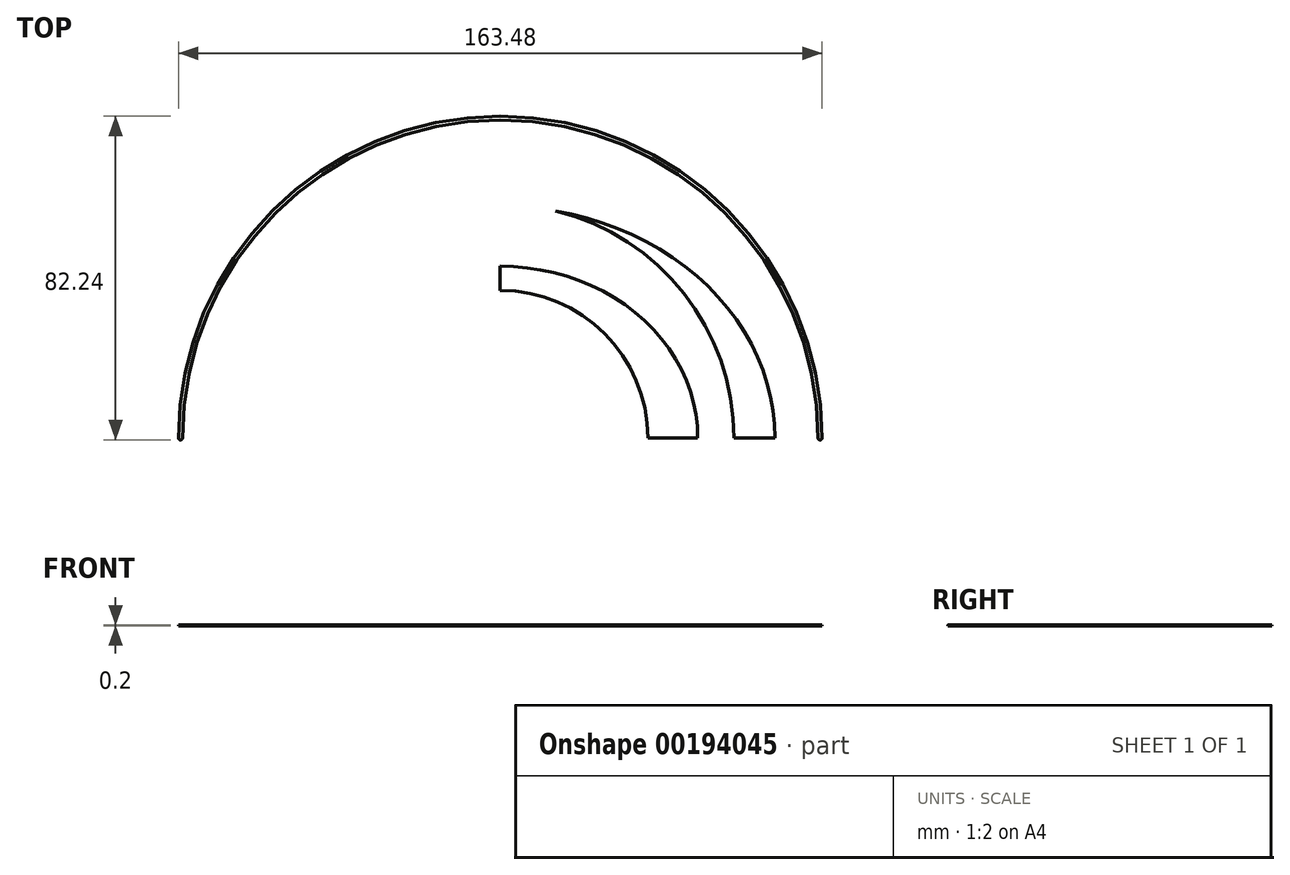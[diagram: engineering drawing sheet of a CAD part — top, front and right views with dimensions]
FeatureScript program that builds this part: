
annotation { "Feature Type Name" : "Feature", "Feature Type Description" : "" }
export const myFeature = defineFeature(function(context is Context, id is Id, definition is map)
    precondition{}
    {
        {
            var Q0;
            Q0=qCreatedBy(makeId("Top.planeOp"),FACE);
            var sketch = newSketch(context, id + "F0", { "sketchPlane" : qUnion([Q0])});
            skArc(sketch, "E0", {"start": v(-125, 0) * mm, "mid": v(0, 125) * mm, "end": v(125, 0) * mm});
            skArc(sketch, "E1", {"start": v(-81.24, 0) * mm, "mid": v(0, 81.24) * mm, "end": v(81.24, 0) * mm});
            skArc(sketch, "E2", {"start": v(-59.35, 0) * mm, "mid": v(0, 59.35) * mm, "end": v(59.35, 0) * mm});
            skArc(sketch, "E3", {"start": v(-37.47, 0) * mm, "mid": v(0, 37.47) * mm, "end": v(37.47, 0) * mm});
            skLineSegment(sketch, "E4", {"start": v(37.47, 0) * mm, "end": v(59.35, 0) * mm});
            skLineSegment(sketch, "E5", {"start": v(59.35, 0) * mm, "end": v(81.24, 0) * mm});
            skLineSegment(sketch, "E6", {"start": v(81.24, 0) * mm, "end": v(103.12, 0) * mm});
            skLineSegment(sketch, "E7", {"start": v(103.12, 0) * mm, "end": v(125, 0) * mm});
            skEllipticalArc(sketch, "E8", {});
            skEllipticalArc(sketch, "E9", {});
            skLineSegment(sketch, "E10", {"start": v(0, 0) * mm, "end": v(-125, 0) * mm});
            skEllipticalArc(sketch, "E11", {});
            skLineSegment(sketch, "E12", {"start": v(0, 0) * mm, "end": v(37.47, 0) * mm});
            skPoint(sketch, "E13", {"position": v(0, 27.98) * mm});
            skPoint(sketch, "E14", {"position": v(0, 37.47) * mm});
            skPoint(sketch, "E15", {"position": v(0, 49.86) * mm});
            skPoint(sketch, "E16", {"position": v(0, 59.35) * mm});
            skPoint(sketch, "E17", {"position": v(0, 71.74) * mm});
            skPoint(sketch, "E18", {"position": v(0, 81.24) * mm});
            skPoint(sketch, "E19", {"position": v(0, 93.62) * mm});
            skPoint(sketch, "E20", {"position": v(0, 125) * mm});
            skLineSegment(sketch, "E21", {"start": v(0, 81.24) * mm, "end": v(0, 93.62) * mm});
            skLineSegment(sketch, "E22", {"start": v(0, 59.35) * mm, "end": v(0, 71.74) * mm});
            skLineSegment(sketch, "E23", {"start": v(0, 37.47) * mm, "end": v(0, 49.86) * mm});
            skLineSegment(sketch, "E24", {"start": v(25.09, 0) * mm, "end": v(37.47, 0) * mm});
            skLineSegment(sketch, "E25", {"start": v(46.97, 0) * mm, "end": v(59.35, 0) * mm});
            skLineSegment(sketch, "E26", {"start": v(68.85, 0) * mm, "end": v(81.24, 0) * mm});
            skLineSegment(sketch, "E27", {"start": v(0, 71.74) * mm, "end": v(0, 49.86) * mm});
            skLineSegment(sketch, "E28", {"start": v(0, 27.98) * mm, "end": v(0, 49.86) * mm});
            const initialGuessF0  = {"E8": [0, 0, 1, 0, 0.0697578449369025, 0.05887321209295041, 0, 3.141592653589793], "E9": [0, 0, -1, 0, 0.05015816765465959, 0.04363105702985292, 3.141592653589793, 0], "E11": [0, 0, 1, 0, 0.03491601259156208, 0.028388901966755413, 0, 3.141592653589793], "E11": [0, 0, 1, 0, 0.01967385752846458, 0.01314674690365791, 0, 3.141592653589793]};
            skSetInitialGuess(sketch, initialGuessF0);
            skSolve(sketch);
        }
        {
            var Q0;
            Q0=qCreatedBy(makeId("Top.planeOp"),FACE);
            var sketch = newSketch(context, id + "F1", { "sketchPlane" : qUnion([Q0])});
            skEllipticalArc(sketch, "E29.0", {});
            skArc(sketch, "E30.0", {"start": v(-81.24, 0) * mm, "mid": v(0, 81.24) * mm, "end": v(81.24, 0) * mm});
            skEllipticalArc(sketch, "E31.0", {});
            skArc(sketch, "E32.0", {"start": v(-59.35, 0) * mm, "mid": v(0, 59.35) * mm, "end": v(59.35, 0) * mm});
            skEllipticalArc(sketch, "E33.0", {});
            skArc(sketch, "E34.0", {"start": v(-37.47, 0) * mm, "mid": v(0, 37.47) * mm, "end": v(37.47, 0) * mm});
            skArc(sketch, "E35.0.startCap", {"start": v(103.62, 0) * mm, "mid": v(103.12, -0.5) * mm, "end": v(102.62, 0) * mm});
            skArc(sketch, "E35.0.endCap", {"start": v(-102.62, 0) * mm, "mid": v(-103.12, -0.5) * mm, "end": v(-103.62, 0) * mm});
            skFitSpline(sketch, "E35.0.left", {"points": [v(82.49, -3.39) * mm, v(82.6, 0) * mm, v(82.49, 3.39) * mm, v(82.09, 7.87) * mm, v(81.09, 13.4) * mm, v(79.12, 19.87) * mm, v(76.4, 26.15) * mm, v(72.96, 32.17) * mm, v(69.5, 36.95) * mm, v(66.4, 40.6) * mm, v(63.9, 43.26) * mm, v(61.24, 45.81) * mm, v(58.41, 48.27) * mm, v(55.44, 50.6) * mm, v(52.36, 52.8) * mm, v(49.15, 54.87) * mm, v(44.73, 57.44) * mm, v(38.95, 60.3) * mm, v(31.66, 63.15) * mm, v(24.06, 65.4) * mm, v(17.53, 66.76) * mm, v(12.2, 67.53) * mm, v(8.17, 67.95) * mm, v(4.78, 68.15) * mm, v(2.05, 68.24) * mm, v(0, 68.26) * mm, v(-2.05, 68.24) * mm, v(-4.78, 68.15) * mm, v(-8.17, 67.95) * mm, v(-12.2, 67.53) * mm, v(-17.53, 66.76) * mm, v(-24.06, 65.4) * mm, v(-31.66, 63.15) * mm, v(-38.95, 60.3) * mm, v(-44.73, 57.44) * mm, v(-49.15, 54.87) * mm, v(-52.36, 52.8) * mm, v(-55.44, 50.6) * mm, v(-58.41, 48.27) * mm, v(-61.24, 45.81) * mm, v(-63.9, 43.26) * mm, v(-66.4, 40.6) * mm, v(-69.5, 36.95) * mm, v(-72.96, 32.17) * mm, v(-76.4, 26.15) * mm, v(-79.12, 19.87) * mm, v(-81.09, 13.4) * mm, v(-82.09, 7.87) * mm, v(-82.49, 3.39) * mm, v(-82.6, 0) * mm, v(-82.49, -3.39) * mm, v(-82.09, -7.87) * mm, v(-81.09, -13.4) * mm, v(-79.12, -19.87) * mm, v(-76.4, -26.15) * mm, v(-72.96, -32.17) * mm, v(-69.5, -36.95) * mm, v(-66.4, -40.6) * mm, v(-63.9, -43.26) * mm, v(-61.24, -45.81) * mm, v(-58.41, -48.27) * mm, v(-55.44, -50.6) * mm, v(-52.36, -52.8) * mm, v(-49.15, -54.87) * mm, v(-44.73, -57.44) * mm, v(-38.95, -60.3) * mm, v(-31.66, -63.15) * mm, v(-24.06, -65.4) * mm, v(-17.53, -66.76) * mm, v(-12.2, -67.53) * mm, v(-8.17, -67.95) * mm, v(-4.78, -68.15) * mm, v(-2.05, -68.24) * mm, v(0, -68.26) * mm, v(2.05, -68.24) * mm, v(4.78, -68.15) * mm, v(8.17, -67.95) * mm, v(12.2, -67.53) * mm, v(17.53, -66.76) * mm, v(24.06, -65.4) * mm, v(31.66, -63.15) * mm, v(38.95, -60.3) * mm, v(44.73, -57.44) * mm, v(49.15, -54.87) * mm, v(52.36, -52.8) * mm, v(55.44, -50.6) * mm, v(58.41, -48.27) * mm, v(61.24, -45.81) * mm, v(63.9, -43.26) * mm, v(66.4, -40.6) * mm, v(69.5, -36.95) * mm, v(72.96, -32.17) * mm, v(76.4, -26.15) * mm, v(79.12, -19.87) * mm, v(81.09, -13.4) * mm, v(82.09, -7.87) * mm, v(82.49, -3.39) * mm, v(82.6, 0) * mm, v(82.49, 3.39) * mm]});
            skFitSpline(sketch, "E35.0.right", {"points": [v(82.89, -3.41) * mm, v(83, 0) * mm, v(82.89, 3.41) * mm, v(82.48, 7.92) * mm, v(81.48, 13.5) * mm, v(79.5, 20.01) * mm, v(76.76, 26.33) * mm, v(73.3, 32.4) * mm, v(69.82, 37.2) * mm, v(66.7, 40.87) * mm, v(64.18, 43.54) * mm, v(61.51, 46.1) * mm, v(58.67, 48.58) * mm, v(55.68, 50.93) * mm, v(52.58, 53.14) * mm, v(49.36, 55.21) * mm, v(44.92, 57.8) * mm, v(39.1, 60.67) * mm, v(31.78, 63.53) * mm, v(24.16, 65.8) * mm, v(17.6, 67.16) * mm, v(12.25, 67.93) * mm, v(8.2, 68.34) * mm, v(4.8, 68.55) * mm, v(2.06, 68.64) * mm, v(0, 68.66) * mm, v(-2.06, 68.64) * mm, v(-4.8, 68.55) * mm, v(-8.2, 68.34) * mm, v(-12.25, 67.93) * mm, v(-17.6, 67.16) * mm, v(-24.16, 65.8) * mm, v(-31.78, 63.53) * mm, v(-39.1, 60.67) * mm, v(-44.92, 57.8) * mm, v(-49.36, 55.21) * mm, v(-52.58, 53.14) * mm, v(-55.68, 50.93) * mm, v(-58.67, 48.58) * mm, v(-61.51, 46.1) * mm, v(-64.18, 43.54) * mm, v(-66.7, 40.87) * mm, v(-69.82, 37.2) * mm, v(-73.3, 32.4) * mm, v(-76.76, 26.33) * mm, v(-79.5, 20.01) * mm, v(-81.48, 13.5) * mm, v(-82.48, 7.92) * mm, v(-82.89, 3.41) * mm, v(-83, 0) * mm, v(-82.89, -3.41) * mm, v(-82.48, -7.92) * mm, v(-81.48, -13.5) * mm, v(-79.5, -20.01) * mm, v(-76.76, -26.33) * mm, v(-73.3, -32.4) * mm, v(-69.82, -37.2) * mm, v(-66.7, -40.87) * mm, v(-64.18, -43.54) * mm, v(-61.51, -46.1) * mm, v(-58.67, -48.58) * mm, v(-55.68, -50.93) * mm, v(-52.58, -53.14) * mm, v(-49.36, -55.21) * mm, v(-44.92, -57.8) * mm, v(-39.1, -60.67) * mm, v(-31.78, -63.53) * mm, v(-24.16, -65.8) * mm, v(-17.6, -67.16) * mm, v(-12.25, -67.93) * mm, v(-8.2, -68.34) * mm, v(-4.8, -68.55) * mm, v(-2.06, -68.64) * mm, v(0, -68.66) * mm, v(2.06, -68.64) * mm, v(4.8, -68.55) * mm, v(8.2, -68.34) * mm, v(12.25, -67.93) * mm, v(17.6, -67.16) * mm, v(24.16, -65.8) * mm, v(31.78, -63.53) * mm, v(39.1, -60.67) * mm, v(44.92, -57.8) * mm, v(49.36, -55.21) * mm, v(52.58, -53.14) * mm, v(55.68, -50.93) * mm, v(58.67, -48.58) * mm, v(61.51, -46.1) * mm, v(64.18, -43.54) * mm, v(66.7, -40.87) * mm, v(69.82, -37.2) * mm, v(73.3, -32.4) * mm, v(76.76, -26.33) * mm, v(79.5, -20.01) * mm, v(81.48, -13.5) * mm, v(82.48, -7.92) * mm, v(82.89, -3.41) * mm, v(83, 0) * mm, v(82.89, 3.41) * mm]});
            skArc(sketch, "E35.3.startCap", {"start": v(-80.74, 0) * mm, "mid": v(-81.24, -0.5) * mm, "end": v(-81.74, 0) * mm});
            skArc(sketch, "E35.3.endCap", {"start": v(81.74, 0) * mm, "mid": v(81.24, -0.5) * mm, "end": v(80.74, 0) * mm});
            skArc(sketch, "E35.3.left", {"start": v(-81.74, 0) * mm, "mid": v(0, 81.74) * mm, "end": v(81.74, 0) * mm});
            skArc(sketch, "E35.3.right", {"start": v(-80.74, 0) * mm, "mid": v(0, 80.74) * mm, "end": v(80.74, 0) * mm});
            skArc(sketch, "E35.4.startCap", {"start": v(25.59, 0) * mm, "mid": v(25.09, -0.5) * mm, "end": v(24.59, 0) * mm});
            skArc(sketch, "E35.4.endCap", {"start": v(-24.59, 0) * mm, "mid": v(-25.09, -0.5) * mm, "end": v(-25.59, 0) * mm});
            skFitSpline(sketch, "E35.4.left", {"points": [v(13.24, -1.06) * mm, v(13.48, 0) * mm, v(13.24, 1.06) * mm, v(12.63, 1.94) * mm, v(11.89, 2.6) * mm, v(11, 3.25) * mm, v(9.6, 3.98) * mm, v(7.9, 4.59) * mm, v(6.37, 4.98) * mm, v(4.77, 5.3) * mm, v(3.08, 5.53) * mm, v(1.33, 5.64) * mm, v(0, 5.67) * mm, v(-1.33, 5.64) * mm, v(-3.08, 5.53) * mm, v(-4.77, 5.3) * mm, v(-6.37, 4.98) * mm, v(-7.9, 4.59) * mm, v(-9.6, 3.98) * mm, v(-11, 3.25) * mm, v(-11.89, 2.6) * mm, v(-12.63, 1.94) * mm, v(-13.24, 1.06) * mm, v(-13.48, 0) * mm, v(-13.24, -1.06) * mm, v(-12.63, -1.94) * mm, v(-11.89, -2.6) * mm, v(-11, -3.25) * mm, v(-9.6, -3.98) * mm, v(-7.9, -4.59) * mm, v(-6.37, -4.98) * mm, v(-4.77, -5.3) * mm, v(-3.08, -5.53) * mm, v(-1.33, -5.64) * mm, v(0, -5.67) * mm, v(1.33, -5.64) * mm, v(3.08, -5.53) * mm, v(4.77, -5.3) * mm, v(6.37, -4.98) * mm, v(7.9, -4.59) * mm, v(9.6, -3.98) * mm, v(11, -3.25) * mm, v(11.89, -2.6) * mm, v(12.63, -1.94) * mm, v(13.24, -1.06) * mm, v(13.48, 0) * mm, v(13.24, 1.06) * mm]});
            skFitSpline(sketch, "E35.4.right", {"points": [v(13.75, -0.62) * mm, v(13.82, 0) * mm, v(13.75, 0.62) * mm, v(13.47, 1.43) * mm, v(12.93, 2.2) * mm, v(12.14, 2.92) * mm, v(11.2, 3.6) * mm, v(9.76, 4.35) * mm, v(8.02, 4.97) * mm, v(6.46, 5.37) * mm, v(4.84, 5.7) * mm, v(3.12, 5.92) * mm, v(1.35, 6.04) * mm, v(0, 6.07) * mm, v(-1.35, 6.04) * mm, v(-3.12, 5.92) * mm, v(-4.84, 5.7) * mm, v(-6.46, 5.37) * mm, v(-8.02, 4.97) * mm, v(-9.76, 4.35) * mm, v(-11.2, 3.6) * mm, v(-12.14, 2.92) * mm, v(-12.93, 2.2) * mm, v(-13.47, 1.43) * mm, v(-13.75, 0.62) * mm, v(-13.82, 0) * mm, v(-13.75, -0.62) * mm, v(-13.47, -1.43) * mm, v(-12.93, -2.2) * mm, v(-12.14, -2.92) * mm, v(-11.2, -3.6) * mm, v(-9.76, -4.35) * mm, v(-8.02, -4.97) * mm, v(-6.46, -5.37) * mm, v(-4.84, -5.7) * mm, v(-3.12, -5.92) * mm, v(-1.35, -6.04) * mm, v(0, -6.07) * mm, v(1.35, -6.04) * mm, v(3.12, -5.92) * mm, v(4.84, -5.7) * mm, v(6.46, -5.37) * mm, v(8.02, -4.97) * mm, v(9.76, -4.35) * mm, v(11.2, -3.6) * mm, v(12.14, -2.92) * mm, v(12.93, -2.2) * mm, v(13.47, -1.43) * mm, v(13.75, -0.62) * mm, v(13.82, 0) * mm, v(13.75, 0.62) * mm]});
            skArc(sketch, "E35.5.startCap", {"start": v(69.35, 0) * mm, "mid": v(68.85, -0.5) * mm, "end": v(68.35, 0) * mm});
            skArc(sketch, "E35.5.endCap", {"start": v(-68.35, 0) * mm, "mid": v(-68.85, -0.5) * mm, "end": v(-69.35, 0) * mm});
            skFitSpline(sketch, "E35.5.left", {"points": [v(-55.09, 2.35) * mm, v(-55.15, 0) * mm, v(-55.09, -2.35) * mm, v(-54.82, -5.46) * mm, v(-54.15, -9.3) * mm, v(-52.83, -13.8) * mm, v(-51.02, -18.15) * mm, v(-48.72, -22.34) * mm, v(-45.95, -26.32) * mm, v(-43.27, -29.44) * mm, v(-40.9, -31.8) * mm, v(-39.01, -33.51) * mm, v(-37.03, -35.13) * mm, v(-34.28, -37.17) * mm, v(-30.64, -39.48) * mm, v(-26.01, -41.87) * mm, v(-21.14, -43.85) * mm, v(-16.07, -45.4) * mm, v(-10.83, -46.54) * mm, v(-6.36, -47.12) * mm, v(-2.74, -47.35) * mm, v(0, -47.4) * mm, v(2.74, -47.35) * mm, v(6.36, -47.12) * mm, v(10.83, -46.54) * mm, v(16.07, -45.4) * mm, v(21.14, -43.85) * mm, v(26.01, -41.87) * mm, v(30.64, -39.48) * mm, v(34.28, -37.17) * mm, v(37.03, -35.13) * mm, v(39.01, -33.51) * mm, v(40.9, -31.8) * mm, v(43.27, -29.44) * mm, v(45.95, -26.32) * mm, v(48.72, -22.34) * mm, v(51.02, -18.15) * mm, v(52.83, -13.8) * mm, v(54.15, -9.3) * mm, v(54.82, -5.46) * mm, v(55.09, -2.35) * mm, v(55.15, 0) * mm, v(55.09, 2.35) * mm, v(54.82, 5.46) * mm, v(54.15, 9.3) * mm, v(52.83, 13.8) * mm, v(51.02, 18.15) * mm, v(48.72, 22.34) * mm, v(45.95, 26.32) * mm, v(43.27, 29.44) * mm, v(40.9, 31.8) * mm, v(39.01, 33.51) * mm, v(37.03, 35.13) * mm, v(34.28, 37.17) * mm, v(30.64, 39.48) * mm, v(26.01, 41.87) * mm, v(21.14, 43.85) * mm, v(16.07, 45.4) * mm, v(10.83, 46.54) * mm, v(6.36, 47.12) * mm, v(2.74, 47.35) * mm, v(0, 47.4) * mm, v(-2.74, 47.35) * mm, v(-6.36, 47.12) * mm, v(-10.83, 46.54) * mm, v(-16.07, 45.4) * mm, v(-21.14, 43.85) * mm, v(-26.01, 41.87) * mm, v(-30.64, 39.48) * mm, v(-34.28, 37.17) * mm, v(-37.03, 35.13) * mm, v(-39.01, 33.51) * mm, v(-40.9, 31.8) * mm, v(-43.27, 29.44) * mm, v(-45.95, 26.32) * mm, v(-48.72, 22.34) * mm, v(-51.02, 18.15) * mm, v(-52.83, 13.8) * mm, v(-54.15, 9.3) * mm, v(-54.82, 5.46) * mm, v(-55.09, 2.35) * mm, v(-55.15, 0) * mm, v(-55.09, -2.35) * mm]});
            skFitSpline(sketch, "E35.5.right", {"points": [v(-55.49, 2.37) * mm, v(-55.55, 0) * mm, v(-55.49, -2.37) * mm, v(-55.21, -5.51) * mm, v(-54.54, -9.4) * mm, v(-53.21, -13.93) * mm, v(-51.38, -18.33) * mm, v(-49.06, -22.55) * mm, v(-46.27, -26.56) * mm, v(-43.56, -29.71) * mm, v(-41.17, -32.1) * mm, v(-39.27, -33.81) * mm, v(-37.27, -35.45) * mm, v(-34.5, -37.5) * mm, v(-30.84, -39.83) * mm, v(-26.18, -42.23) * mm, v(-21.27, -44.22) * mm, v(-16.17, -45.8) * mm, v(-10.9, -46.94) * mm, v(-6.4, -47.51) * mm, v(-2.76, -47.75) * mm, v(0, -47.8) * mm, v(2.76, -47.75) * mm, v(6.4, -47.51) * mm, v(10.9, -46.94) * mm, v(16.17, -45.8) * mm, v(21.27, -44.22) * mm, v(26.18, -42.23) * mm, v(30.84, -39.83) * mm, v(34.5, -37.5) * mm, v(37.27, -35.45) * mm, v(39.27, -33.81) * mm, v(41.17, -32.1) * mm, v(43.56, -29.71) * mm, v(46.27, -26.56) * mm, v(49.06, -22.55) * mm, v(51.38, -18.33) * mm, v(53.21, -13.93) * mm, v(54.54, -9.4) * mm, v(55.21, -5.51) * mm, v(55.49, -2.37) * mm, v(55.55, 0) * mm, v(55.49, 2.37) * mm, v(55.21, 5.51) * mm, v(54.54, 9.4) * mm, v(53.21, 13.93) * mm, v(51.38, 18.33) * mm, v(49.06, 22.55) * mm, v(46.27, 26.56) * mm, v(43.56, 29.71) * mm, v(41.17, 32.1) * mm, v(39.27, 33.81) * mm, v(37.27, 35.45) * mm, v(34.5, 37.5) * mm, v(30.84, 39.83) * mm, v(26.18, 42.23) * mm, v(21.27, 44.22) * mm, v(16.17, 45.8) * mm, v(10.9, 46.94) * mm, v(6.4, 47.51) * mm, v(2.76, 47.75) * mm, v(0, 47.8) * mm, v(-2.76, 47.75) * mm, v(-6.4, 47.51) * mm, v(-10.9, 46.94) * mm, v(-16.17, 45.8) * mm, v(-21.27, 44.22) * mm, v(-26.18, 42.23) * mm, v(-30.84, 39.83) * mm, v(-34.5, 37.5) * mm, v(-37.27, 35.45) * mm, v(-39.27, 33.81) * mm, v(-41.17, 32.1) * mm, v(-43.56, 29.71) * mm, v(-46.27, 26.56) * mm, v(-49.06, 22.55) * mm, v(-51.38, 18.33) * mm, v(-53.21, 13.93) * mm, v(-54.54, 9.4) * mm, v(-55.21, 5.51) * mm, v(-55.49, 2.37) * mm, v(-55.55, 0) * mm, v(-55.49, -2.37) * mm]});
            skArc(sketch, "E35.6.startCap", {"start": v(-36.97, 0) * mm, "mid": v(-37.47, -0.5) * mm, "end": v(-37.97, 0) * mm});
            skArc(sketch, "E35.6.endCap", {"start": v(37.97, 0) * mm, "mid": v(37.47, -0.5) * mm, "end": v(36.97, 0) * mm});
            skArc(sketch, "E35.6.left", {"start": v(-37.97, 0) * mm, "mid": v(0, 37.97) * mm, "end": v(37.97, 0) * mm});
            skArc(sketch, "E35.6.right", {"start": v(-36.97, 0) * mm, "mid": v(0, 36.97) * mm, "end": v(36.97, 0) * mm});
            skArc(sketch, "E35.7.startCap", {"start": v(-58.85, 0) * mm, "mid": v(-59.35, -0.5) * mm, "end": v(-59.85, 0) * mm});
            skArc(sketch, "E35.7.endCap", {"start": v(59.85, 0) * mm, "mid": v(59.35, -0.5) * mm, "end": v(58.85, 0) * mm});
            skArc(sketch, "E35.7.left", {"start": v(-59.85, 0) * mm, "mid": v(0, 59.85) * mm, "end": v(59.85, 0) * mm});
            skArc(sketch, "E35.7.right", {"start": v(-58.85, 0) * mm, "mid": v(0, 58.85) * mm, "end": v(58.85, 0) * mm});
            skArc(sketch, "E35.8.startCap", {"start": v(47.47, 0) * mm, "mid": v(46.97, -0.5) * mm, "end": v(46.47, 0) * mm});
            skArc(sketch, "E35.8.endCap", {"start": v(-46.47, 0) * mm, "mid": v(-46.97, -0.5) * mm, "end": v(-47.47, 0) * mm});
            skFitSpline(sketch, "E35.8.left", {"points": [v(34.24, -1.31) * mm, v(34.28, 0) * mm, v(34.24, 1.31) * mm, v(34.07, 3.05) * mm, v(33.66, 5.2) * mm, v(32.84, 7.71) * mm, v(31.72, 10.15) * mm, v(30.29, 12.49) * mm, v(28.57, 14.72) * mm, v(26.9, 16.47) * mm, v(25.43, 17.79) * mm, v(24.26, 18.74) * mm, v(23.03, 19.65) * mm, v(21.32, 20.8) * mm, v(19.06, 22.1) * mm, v(16.18, 23.43) * mm, v(13.15, 24.54) * mm, v(10, 25.41) * mm, v(6.74, 26.05) * mm, v(3.96, 26.37) * mm, v(1.7, 26.5) * mm, v(0, 26.53) * mm, v(-1.7, 26.5) * mm, v(-3.96, 26.37) * mm, v(-6.74, 26.05) * mm, v(-10, 25.41) * mm, v(-13.15, 24.54) * mm, v(-16.18, 23.43) * mm, v(-19.06, 22.1) * mm, v(-21.32, 20.8) * mm, v(-23.03, 19.65) * mm, v(-24.26, 18.74) * mm, v(-25.43, 17.79) * mm, v(-26.9, 16.47) * mm, v(-28.57, 14.72) * mm, v(-30.29, 12.49) * mm, v(-31.72, 10.15) * mm, v(-32.84, 7.71) * mm, v(-33.66, 5.2) * mm, v(-34.07, 3.05) * mm, v(-34.24, 1.31) * mm, v(-34.28, 0) * mm, v(-34.24, -1.31) * mm, v(-34.07, -3.05) * mm, v(-33.66, -5.2) * mm, v(-32.84, -7.71) * mm, v(-31.72, -10.15) * mm, v(-30.29, -12.49) * mm, v(-28.57, -14.72) * mm, v(-26.9, -16.47) * mm, v(-25.43, -17.79) * mm, v(-24.26, -18.74) * mm, v(-23.03, -19.65) * mm, v(-21.32, -20.8) * mm, v(-19.06, -22.1) * mm, v(-16.18, -23.43) * mm, v(-13.15, -24.54) * mm, v(-10, -25.41) * mm, v(-6.74, -26.05) * mm, v(-3.96, -26.37) * mm, v(-1.7, -26.5) * mm, v(0, -26.53) * mm, v(1.7, -26.5) * mm, v(3.96, -26.37) * mm, v(6.74, -26.05) * mm, v(10, -25.41) * mm, v(13.15, -24.54) * mm, v(16.18, -23.43) * mm, v(19.06, -22.1) * mm, v(21.32, -20.8) * mm, v(23.03, -19.65) * mm, v(24.26, -18.74) * mm, v(25.43, -17.79) * mm, v(26.9, -16.47) * mm, v(28.57, -14.72) * mm, v(30.29, -12.49) * mm, v(31.72, -10.15) * mm, v(32.84, -7.71) * mm, v(33.66, -5.2) * mm, v(34.07, -3.05) * mm, v(34.24, -1.31) * mm, v(34.28, 0) * mm, v(34.24, 1.31) * mm]});
            skFitSpline(sketch, "E35.8.right", {"points": [v(34.64, -1.34) * mm, v(34.68, 0) * mm, v(34.64, 1.34) * mm, v(34.47, 3.11) * mm, v(34.04, 5.3) * mm, v(33.21, 7.86) * mm, v(32.07, 10.34) * mm, v(30.62, 12.72) * mm, v(28.87, 14.98) * mm, v(27.18, 16.75) * mm, v(25.7, 18.1) * mm, v(24.5, 19.06) * mm, v(23.26, 19.98) * mm, v(21.53, 21.14) * mm, v(19.24, 22.45) * mm, v(16.33, 23.8) * mm, v(13.27, 24.92) * mm, v(10.09, 25.8) * mm, v(6.8, 26.44) * mm, v(4, 26.77) * mm, v(1.72, 26.9) * mm, v(0, 26.93) * mm, v(-1.72, 26.9) * mm, v(-4, 26.77) * mm, v(-6.8, 26.44) * mm, v(-10.09, 25.8) * mm, v(-13.27, 24.92) * mm, v(-16.33, 23.8) * mm, v(-19.24, 22.45) * mm, v(-21.53, 21.14) * mm, v(-23.26, 19.98) * mm, v(-24.5, 19.06) * mm, v(-25.7, 18.1) * mm, v(-27.18, 16.75) * mm, v(-28.87, 14.98) * mm, v(-30.62, 12.72) * mm, v(-32.07, 10.34) * mm, v(-33.21, 7.86) * mm, v(-34.04, 5.3) * mm, v(-34.47, 3.11) * mm, v(-34.64, 1.34) * mm, v(-34.68, 0) * mm, v(-34.64, -1.34) * mm, v(-34.47, -3.11) * mm, v(-34.04, -5.3) * mm, v(-33.21, -7.86) * mm, v(-32.07, -10.34) * mm, v(-30.62, -12.72) * mm, v(-28.87, -14.98) * mm, v(-27.18, -16.75) * mm, v(-25.7, -18.1) * mm, v(-24.5, -19.06) * mm, v(-23.26, -19.98) * mm, v(-21.53, -21.14) * mm, v(-19.24, -22.45) * mm, v(-16.33, -23.8) * mm, v(-13.27, -24.92) * mm, v(-10.09, -25.8) * mm, v(-6.8, -26.44) * mm, v(-4, -26.77) * mm, v(-1.72, -26.9) * mm, v(0, -26.93) * mm, v(1.72, -26.9) * mm, v(4, -26.77) * mm, v(6.8, -26.44) * mm, v(10.09, -25.8) * mm, v(13.27, -24.92) * mm, v(16.33, -23.8) * mm, v(19.24, -22.45) * mm, v(21.53, -21.14) * mm, v(23.26, -19.98) * mm, v(24.5, -19.06) * mm, v(25.7, -18.1) * mm, v(27.18, -16.75) * mm, v(28.87, -14.98) * mm, v(30.62, -12.72) * mm, v(32.07, -10.34) * mm, v(33.21, -7.86) * mm, v(34.04, -5.3) * mm, v(34.47, -3.11) * mm, v(34.64, -1.34) * mm, v(34.68, 0) * mm, v(34.64, 1.34) * mm]});
            const initialGuessF1  = {"E29.0": [0, 0, 1, 0, 0.08275722200183241, 0.06845269549475103, 0, 3.141592653589793], "E31.0": [0, 0, -1, 0, 0.055330932086608546, 0.0475872872835984, 3.141592653589793, 0], "E33.0": [0, 0, 1, 0, 0.03446552387545592, 0.026721879072445772, 0, 3.141592653589793], "E33.0": [0, 0, 1, 0, 0.013600115664303296, 0.0058564708612931435, 0, 3.141592653589793]};
            skSetInitialGuess(sketch, initialGuessF1);
            skSolve(sketch);
        }
        {
            var Q0;
            {var subQ0=sQuery(id+"F0.wireOp",EDGE,"E24");Q0=makeQuery(id+"F0.imprint","IMPRINT",FACE,{"disambiguationData":[TD([[makeQuery(id+"F0.imprint","IMPRINT",EDGE,{"derivedFrom":subQ0}),1.0]])]});}
            var Q1;
            {var subQ0=sQuery(id+"F0.wireOp",EDGE,"E4");Q1=makeQuery(id+"F0.imprint","IMPRINT",FACE,{"disambiguationData":[TD([[makeQuery(id+"F0.imprint","IMPRINT",EDGE,{"derivedFrom":subQ0}),1.0]])]});}
            var Q2;
            {var subQ0=sQuery(id+"F0.wireOp",EDGE,"E25");Q2=makeQuery(id+"F0.imprint","IMPRINT",FACE,{"disambiguationData":[TD([[makeQuery(id+"F0.imprint","IMPRINT",EDGE,{"derivedFrom":subQ0}),1.0]])]});}
            var Q3;
            {var subQ0=sQuery(id+"F0.wireOp",EDGE,"E5");Q3=makeQuery(id+"F0.imprint","IMPRINT",FACE,{"disambiguationData":[TD([[makeQuery(id+"F0.imprint","IMPRINT",EDGE,{"derivedFrom":subQ0}),1.0]])]});}
            var Q4;
            {var subQ0=sQuery(id+"F0.wireOp",EDGE,"E10");var subQ1=sQuery(id+"F0.wireOp",EDGE,"E2");var subQ2=makeQuery(id+"F0.imprint","INTERSECT",VERTEX,{"derivedFrom":[subQ1,subQ0]});Q4=makeQuery(id+"F0.imprint","IMPRINT",FACE,{"disambiguationData":[TD([[makeQuery(id+"F0.imprint","IMPRINT",EDGE,{"disambiguationData":[TD([[subQ2,-1.0]])],"derivedFrom":subQ1}),1.0]])]});}
            var Q5;
            {var subQ3=sQuery(id+"F1.wireOp",EDGE,"E35.7.left");var subQ5=sQuery(id+"F1.wireOp",EDGE,"E35.2.right");var subQ6=makeQuery(id+"F1.imprint","INTERSECT",VERTEX,{"derivedFrom":[subQ5,subQ3]});Q5=makeQuery(id+"F1.imprint","IMPRINT",FACE,{"disambiguationData":[TD([[makeQuery(id+"F1.imprint","IMPRINT",EDGE,{"disambiguationData":[TD([[subQ6,-1.0]])],"derivedFrom":subQ5}),1.0]])]});}
            var Q6;
            {var subQ0=sQuery(id+"F1.wireOp",EDGE,"E35.2.right");var subQ1=sQuery(id+"F1.wireOp",EDGE,"E32.0");var subQ2=makeQuery(id+"F1.imprint","INTERSECT",VERTEX,{"derivedFrom":[subQ1,subQ0]});Q6=makeQuery(id+"F1.imprint","IMPRINT",FACE,{"disambiguationData":[TD([[makeQuery(id+"F1.imprint","IMPRINT",EDGE,{"disambiguationData":[TD([[subQ2,-1.0]])],"derivedFrom":subQ1}),1.0]])]});}
            var Q7;
            {var subQ0=sQuery(id+"F1.wireOp",EDGE,"52e85f9d-6710-4ef4-a348-8d421ddb169b.0.left");var subQ1=sQuery(id+"F1.wireOp",EDGE,"E29.0");var subQ2=makeQuery(id+"F1.imprint","INTERSECT",VERTEX,{"derivedFrom":[subQ1,subQ0]});Q7=makeQuery(id+"F1.imprint","IMPRINT",FACE,{"disambiguationData":[TD([[makeQuery(id+"F1.imprint","IMPRINT",EDGE,{"disambiguationData":[TD([[subQ2,-1.0]])],"derivedFrom":subQ1}),1.0]])]});}
            var Q8;
            {var subQ1=sQuery(id+"F1.wireOp",EDGE,"E35.0.right");var subQ3=sQuery(id+"F1.wireOp",EDGE,"52e85f9d-6710-4ef4-a348-8d421ddb169b.0.left");var subQ4=makeQuery(id+"F1.imprint","INTERSECT",VERTEX,{"derivedFrom":[subQ1,subQ3]});Q8=makeQuery(id+"F1.imprint","IMPRINT",FACE,{"disambiguationData":[TD([[makeQuery(id+"F1.imprint","IMPRINT",EDGE,{"disambiguationData":[TD([[subQ4,-1.0]])],"derivedFrom":subQ3}),-1.0]])]});}
            var Q9;
            {var subQ0=sQuery(id+"F1.wireOp",EDGE,"52e85f9d-6710-4ef4-a348-8d421ddb169b.0.left");var subQ1=sQuery(id+"F1.wireOp",EDGE,"E29.0");var subQ2=makeQuery(id+"F1.imprint","INTERSECT",VERTEX,{"derivedFrom":[subQ1,subQ0]});Q9=makeQuery(id+"F1.imprint","IMPRINT",FACE,{"disambiguationData":[TD([[makeQuery(id+"F1.imprint","IMPRINT",EDGE,{"disambiguationData":[TD([[subQ2,-1.0]])],"derivedFrom":subQ1}),-1.0]])]});}
            var Q10;
            {var subQ1=sQuery(id+"F1.wireOp",EDGE,"E35.7.right");var subQ3=sQuery(id+"F1.wireOp",EDGE,"52e85f9d-6710-4ef4-a348-8d421ddb169b.0.left");var subQ4=makeQuery(id+"F1.imprint","INTERSECT",VERTEX,{"derivedFrom":[subQ1,subQ3]});Q10=makeQuery(id+"F1.imprint","IMPRINT",FACE,{"disambiguationData":[TD([[makeQuery(id+"F1.imprint","IMPRINT",EDGE,{"disambiguationData":[TD([[subQ4,1.0]])],"derivedFrom":subQ3}),-1.0]])]});}
            var Q11;
            {var subQ1=sQuery(id+"F1.wireOp",EDGE,"E35.4.right");var subQ3=sQuery(id+"F1.wireOp",EDGE,"52e85f9d-6710-4ef4-a348-8d421ddb169b.0.left");var subQ4=makeQuery(id+"F1.imprint","INTERSECT",VERTEX,{"derivedFrom":[subQ1,subQ3]});Q11=makeQuery(id+"F1.imprint","IMPRINT",FACE,{"disambiguationData":[TD([[makeQuery(id+"F1.imprint","IMPRINT",EDGE,{"disambiguationData":[TD([[subQ4,-1.0]])],"derivedFrom":subQ3}),-1.0]])]});}
            var Q12;
            {var subQ0=sQuery(id+"F1.wireOp",EDGE,"52e85f9d-6710-4ef4-a348-8d421ddb169b.0.left");var subQ1=sQuery(id+"F1.wireOp",EDGE,"E33.0");var subQ2=makeQuery(id+"F1.imprint","INTERSECT",VERTEX,{"derivedFrom":[subQ1,subQ0]});Q12=makeQuery(id+"F1.imprint","IMPRINT",FACE,{"disambiguationData":[TD([[makeQuery(id+"F1.imprint","IMPRINT",EDGE,{"disambiguationData":[TD([[subQ2,-1.0]])],"derivedFrom":subQ1}),-1.0]])]});}
            var Q13;
            {var subQ0=sQuery(id+"F1.wireOp",EDGE,"52e85f9d-6710-4ef4-a348-8d421ddb169b.0.left");var subQ5=sQuery(id+"F1.wireOp",EDGE,"E35.4.left");var subQ7=makeQuery(id+"F1.imprint","INTERSECT",VERTEX,{"derivedFrom":[subQ5,subQ0]});Q13=makeQuery(id+"F1.imprint","IMPRINT",FACE,{"disambiguationData":[TD([[makeQuery(id+"F1.imprint","IMPRINT",EDGE,{"disambiguationData":[TD([[subQ7,1.0]])],"derivedFrom":subQ5}),1.0]])]});}
            var Q14;
            {var subQ0=sQuery(id+"F1.wireOp",EDGE,"E35.6.left");var subQ5=sQuery(id+"F1.wireOp",EDGE,"E35.2.right");var subQ6=makeQuery(id+"F1.imprint","INTERSECT",VERTEX,{"derivedFrom":[subQ5,subQ0]});Q14=makeQuery(id+"F1.imprint","IMPRINT",FACE,{"disambiguationData":[TD([[makeQuery(id+"F1.imprint","IMPRINT",EDGE,{"disambiguationData":[TD([[subQ6,-1.0]])],"derivedFrom":subQ5}),1.0]])]});}
            var Q15;
            {var subQ0=sQuery(id+"F1.wireOp",EDGE,"52e85f9d-6710-4ef4-a348-8d421ddb169b.0.left");var subQ1=sQuery(id+"F1.wireOp",EDGE,"E31.0");var subQ2=makeQuery(id+"F1.imprint","INTERSECT",VERTEX,{"derivedFrom":[subQ1,subQ0]});Q15=makeQuery(id+"F1.imprint","IMPRINT",FACE,{"disambiguationData":[TD([[makeQuery(id+"F1.imprint","IMPRINT",EDGE,{"disambiguationData":[TD([[subQ2,-1.0]])],"derivedFrom":subQ1}),1.0]])]});}
            var Q16;
            {var subQ0=sQuery(id+"F1.wireOp",EDGE,"E35.2.right");var subQ1=sQuery(id+"F1.wireOp",EDGE,"E30.0");var subQ2=makeQuery(id+"F1.imprint","INTERSECT",VERTEX,{"derivedFrom":[subQ1,subQ0]});Q16=makeQuery(id+"F1.imprint","IMPRINT",FACE,{"disambiguationData":[TD([[makeQuery(id+"F1.imprint","IMPRINT",EDGE,{"disambiguationData":[TD([[subQ2,-1.0]])],"derivedFrom":subQ1}),-1.0]])]});}
            var Q17;
            {var subQ0=sQuery(id+"F1.wireOp",EDGE,"E35.0.right");var subQ5=sQuery(id+"F1.wireOp",EDGE,"E35.2.right");var subQ6=makeQuery(id+"F1.imprint","INTERSECT",VERTEX,{"derivedFrom":[subQ0,subQ5]});Q17=makeQuery(id+"F1.imprint","IMPRINT",FACE,{"disambiguationData":[TD([[makeQuery(id+"F1.imprint","IMPRINT",EDGE,{"disambiguationData":[TD([[subQ6,-1.0]])],"derivedFrom":subQ5}),1.0]])]});}
            var Q18;
            {var subQ5=sQuery(id+"F1.wireOp",EDGE,"E35.1.left");Q18=makeQuery(id+"F1.imprint","IMPRINT",FACE,{"disambiguationData":[TD([[makeQuery(id+"F1.imprint","IMPRINT",EDGE,{"derivedFrom":subQ5}),-1.0]])]});}
            var Q19;
            {var subQ0=sQuery(id+"F1.wireOp",EDGE,"E35.2.right");var subQ1=sQuery(id+"F1.wireOp",EDGE,"d5c510f4-37f1-434f-946f-66e03c4c81df.0");var subQ2=makeQuery(id+"F1.imprint","INTERSECT",VERTEX,{"derivedFrom":[subQ1,subQ0]});Q19=makeQuery(id+"F1.imprint","IMPRINT",FACE,{"disambiguationData":[TD([[makeQuery(id+"F1.imprint","IMPRINT",EDGE,{"disambiguationData":[TD([[subQ2,-1.0]])],"derivedFrom":subQ1}),-1.0]])]});}
            var Q20;
            {var subQ0=sQuery(id+"F1.wireOp",EDGE,"52e85f9d-6710-4ef4-a348-8d421ddb169b.0.left");var subQ1=sQuery(id+"F1.wireOp",EDGE,"E31.0");var subQ2=makeQuery(id+"F1.imprint","INTERSECT",VERTEX,{"derivedFrom":[subQ1,subQ0]});Q20=makeQuery(id+"F1.imprint","IMPRINT",FACE,{"disambiguationData":[TD([[makeQuery(id+"F1.imprint","IMPRINT",EDGE,{"disambiguationData":[TD([[subQ2,-1.0]])],"derivedFrom":subQ1}),-1.0]])]});}
            var Q21;
            {var subQ0=sQuery(id+"F1.wireOp",EDGE,"E35.2.right");var subQ1=sQuery(id+"F1.wireOp",EDGE,"E30.0");var subQ2=makeQuery(id+"F1.imprint","INTERSECT",VERTEX,{"derivedFrom":[subQ1,subQ0]});Q21=makeQuery(id+"F1.imprint","IMPRINT",FACE,{"disambiguationData":[TD([[makeQuery(id+"F1.imprint","IMPRINT",EDGE,{"disambiguationData":[TD([[subQ2,-1.0]])],"derivedFrom":subQ1}),1.0]])]});}
            var Q22;
            {var subQ1=sQuery(id+"F1.wireOp",EDGE,"E35.5.left");var subQ3=sQuery(id+"F1.wireOp",EDGE,"52e85f9d-6710-4ef4-a348-8d421ddb169b.0.left");var subQ4=makeQuery(id+"F1.imprint","INTERSECT",VERTEX,{"derivedFrom":[subQ1,subQ3]});Q22=makeQuery(id+"F1.imprint","IMPRINT",FACE,{"disambiguationData":[TD([[makeQuery(id+"F1.imprint","IMPRINT",EDGE,{"disambiguationData":[TD([[subQ4,1.0]])],"derivedFrom":subQ3}),-1.0]])]});}
            var Q23;
            {var subQ1=sQuery(id+"F1.wireOp",EDGE,"E35.6.left");var subQ3=sQuery(id+"F1.wireOp",EDGE,"52e85f9d-6710-4ef4-a348-8d421ddb169b.0.left");var subQ4=makeQuery(id+"F1.imprint","INTERSECT",VERTEX,{"derivedFrom":[subQ1,subQ3]});Q23=makeQuery(id+"F1.imprint","IMPRINT",FACE,{"disambiguationData":[TD([[makeQuery(id+"F1.imprint","IMPRINT",EDGE,{"disambiguationData":[TD([[subQ4,-1.0]])],"derivedFrom":subQ3}),-1.0]])]});}
            var Q24;
            {var subQ0=sQuery(id+"F1.wireOp",EDGE,"52e85f9d-6710-4ef4-a348-8d421ddb169b.0.left");var subQ1=sQuery(id+"F1.wireOp",EDGE,"E33.0");var subQ2=makeQuery(id+"F1.imprint","INTERSECT",VERTEX,{"derivedFrom":[subQ1,subQ0]});Q24=makeQuery(id+"F1.imprint","IMPRINT",FACE,{"disambiguationData":[TD([[makeQuery(id+"F1.imprint","IMPRINT",EDGE,{"disambiguationData":[TD([[subQ2,-1.0]])],"derivedFrom":subQ1}),-1.0]])]});}
            var Q25;
            {var subQ0=sQuery(id+"F1.wireOp",EDGE,"E35.2.right");var subQ1=sQuery(id+"F1.wireOp",EDGE,"E32.0");var subQ2=makeQuery(id+"F1.imprint","INTERSECT",VERTEX,{"derivedFrom":[subQ1,subQ0]});Q25=makeQuery(id+"F1.imprint","IMPRINT",FACE,{"disambiguationData":[TD([[makeQuery(id+"F1.imprint","IMPRINT",EDGE,{"disambiguationData":[TD([[subQ2,-1.0]])],"derivedFrom":subQ1}),-1.0]])]});}
            var Q26;
            {var subQ0=sQuery(id+"F1.wireOp",EDGE,"E35.2.right");var subQ1=sQuery(id+"F1.wireOp",EDGE,"E34.0");var subQ2=makeQuery(id+"F1.imprint","INTERSECT",VERTEX,{"derivedFrom":[subQ1,subQ0]});Q26=makeQuery(id+"F1.imprint","IMPRINT",FACE,{"disambiguationData":[TD([[makeQuery(id+"F1.imprint","IMPRINT",EDGE,{"disambiguationData":[TD([[subQ2,-1.0]])],"derivedFrom":subQ1}),-1.0]])]});}
            var Q27;
            {var subQ0=sQuery(id+"F1.wireOp",EDGE,"E35.0.left");var subQ5=sQuery(id+"F1.wireOp",EDGE,"E35.2.right");var subQ6=makeQuery(id+"F1.imprint","INTERSECT",VERTEX,{"derivedFrom":[subQ0,subQ5]});Q27=makeQuery(id+"F1.imprint","IMPRINT",FACE,{"disambiguationData":[TD([[makeQuery(id+"F1.imprint","IMPRINT",EDGE,{"disambiguationData":[TD([[subQ6,1.0]])],"derivedFrom":subQ5}),1.0]])]});}
            var Q28;
            {var subQ0=sQuery(id+"F1.wireOp",EDGE,"52e85f9d-6710-4ef4-a348-8d421ddb169b.0.left");var subQ1=sQuery(id+"F1.wireOp",EDGE,"E33.0");var subQ2=makeQuery(id+"F1.imprint","INTERSECT",VERTEX,{"derivedFrom":[subQ1,subQ0]});Q28=makeQuery(id+"F1.imprint","IMPRINT",FACE,{"disambiguationData":[TD([[makeQuery(id+"F1.imprint","IMPRINT",EDGE,{"disambiguationData":[TD([[subQ2,-1.0]])],"derivedFrom":subQ1}),1.0]])]});}
            var Q29;
            {var subQ1=sQuery(id+"F1.wireOp",EDGE,"E35.0.left");var subQ3=sQuery(id+"F1.wireOp",EDGE,"52e85f9d-6710-4ef4-a348-8d421ddb169b.0.left");var subQ4=makeQuery(id+"F1.imprint","INTERSECT",VERTEX,{"derivedFrom":[subQ1,subQ3]});Q29=makeQuery(id+"F1.imprint","IMPRINT",FACE,{"disambiguationData":[TD([[makeQuery(id+"F1.imprint","IMPRINT",EDGE,{"disambiguationData":[TD([[subQ4,1.0]])],"derivedFrom":subQ3}),-1.0]])]});}
            var Q30;
            {var subQ0=sQuery(id+"F1.wireOp",EDGE,"E35.2.right");var subQ1=sQuery(id+"F1.wireOp",EDGE,"E34.0");var subQ2=makeQuery(id+"F1.imprint","INTERSECT",VERTEX,{"derivedFrom":[subQ1,subQ0]});Q30=makeQuery(id+"F1.imprint","IMPRINT",FACE,{"disambiguationData":[TD([[makeQuery(id+"F1.imprint","IMPRINT",EDGE,{"disambiguationData":[TD([[subQ2,-1.0]])],"derivedFrom":subQ1}),1.0]])]});}
            var Q31;
            {var subQ0=sQuery(id+"F1.wireOp",EDGE,"52e85f9d-6710-4ef4-a348-8d421ddb169b.0.left");var subQ1=sQuery(id+"F1.wireOp",EDGE,"E33.0");var subQ2=makeQuery(id+"F1.imprint","INTERSECT",VERTEX,{"derivedFrom":[subQ1,subQ0]});Q31=makeQuery(id+"F1.imprint","IMPRINT",FACE,{"disambiguationData":[TD([[makeQuery(id+"F1.imprint","IMPRINT",EDGE,{"disambiguationData":[TD([[subQ2,-1.0]])],"derivedFrom":subQ1}),1.0]])]});}
            var Q32;
            {var subQ1=sQuery(id+"F1.wireOp",EDGE,"11422904-8dbc-437f-b2cb-607545d81d6e.0");var subQ3=sQuery(id+"F1.wireOp",EDGE,"52e85f9d-6710-4ef4-a348-8d421ddb169b.0.startCap");var subQ4=makeQuery(id+"F1.imprint","INTERSECT",VERTEX,{"derivedFrom":[subQ1,subQ3]});Q32=makeQuery(id+"F1.imprint","IMPRINT",FACE,{"disambiguationData":[TD([[makeQuery(id+"F1.imprint","IMPRINT",EDGE,{"disambiguationData":[TD([[subQ4,-1.0]])],"derivedFrom":subQ1}),-1.0]])]});}
            var Q33;
            {var subQ1=sQuery(id+"F1.wireOp",EDGE,"E35.5.startCap");var subQ3=sQuery(id+"F1.wireOp",EDGE,"52e85f9d-6710-4ef4-a348-8d421ddb169b.0.right");var subQ4=makeQuery(id+"F1.imprint","INTERSECT",VERTEX,{"derivedFrom":[subQ1,subQ3]});Q33=makeQuery(id+"F1.imprint","IMPRINT",FACE,{"disambiguationData":[TD([[makeQuery(id+"F1.imprint","IMPRINT",EDGE,{"disambiguationData":[TD([[subQ4,1.0]])],"derivedFrom":subQ3}),1.0]])]});}
            var Q34;
            {var subQ0=sQuery(id+"F1.wireOp",EDGE,"E35.4.right");var subQ5=sQuery(id+"F1.wireOp",EDGE,"E35.2.right");var subQ6=makeQuery(id+"F1.imprint","INTERSECT",VERTEX,{"derivedFrom":[subQ5,subQ0]});Q34=makeQuery(id+"F1.imprint","IMPRINT",FACE,{"disambiguationData":[TD([[makeQuery(id+"F1.imprint","IMPRINT",EDGE,{"disambiguationData":[TD([[subQ6,-1.0]])],"derivedFrom":subQ5}),1.0]])]});}
            var Q35;
            {var subQ1=sQuery(id+"F1.wireOp",EDGE,"E35.6.endCap");var subQ3=sQuery(id+"F1.wireOp",EDGE,"52e85f9d-6710-4ef4-a348-8d421ddb169b.0.right");var subQ4=makeQuery(id+"F1.imprint","INTERSECT",VERTEX,{"derivedFrom":[subQ1,subQ3]});Q35=makeQuery(id+"F1.imprint","IMPRINT",FACE,{"disambiguationData":[TD([[makeQuery(id+"F1.imprint","IMPRINT",EDGE,{"disambiguationData":[TD([[subQ4,-1.0]])],"derivedFrom":subQ3}),1.0]])]});}
            var Q36;
            {var subQ1=sQuery(id+"F1.wireOp",EDGE,"E35.0.startCap");var subQ3=sQuery(id+"F1.wireOp",EDGE,"52e85f9d-6710-4ef4-a348-8d421ddb169b.0.right");var subQ4=makeQuery(id+"F1.imprint","INTERSECT",VERTEX,{"derivedFrom":[subQ1,subQ3]});Q36=makeQuery(id+"F1.imprint","IMPRINT",FACE,{"disambiguationData":[TD([[makeQuery(id+"F1.imprint","IMPRINT",EDGE,{"disambiguationData":[TD([[subQ4,1.0]])],"derivedFrom":subQ3}),1.0]])]});}
            var Q37;
            {var subQ1=sQuery(id+"F1.wireOp",EDGE,"E35.7.endCap");var subQ3=sQuery(id+"F1.wireOp",EDGE,"52e85f9d-6710-4ef4-a348-8d421ddb169b.0.right");var subQ4=makeQuery(id+"F1.imprint","INTERSECT",VERTEX,{"derivedFrom":[subQ1,subQ3]});Q37=makeQuery(id+"F1.imprint","IMPRINT",FACE,{"disambiguationData":[TD([[makeQuery(id+"F1.imprint","IMPRINT",EDGE,{"disambiguationData":[TD([[subQ4,1.0]])],"derivedFrom":subQ3}),1.0]])]});}
            var Q38;
            {var subQ0=sQuery(id+"F1.wireOp",EDGE,"52e85f9d-6710-4ef4-a348-8d421ddb169b.0.right");var subQ5=sQuery(id+"F1.wireOp",EDGE,"E35.4.startCap");var subQ7=makeQuery(id+"F1.imprint","INTERSECT",VERTEX,{"derivedFrom":[subQ5,subQ0]});Q38=makeQuery(id+"F1.imprint","IMPRINT",FACE,{"disambiguationData":[TD([[makeQuery(id+"F1.imprint","IMPRINT",EDGE,{"disambiguationData":[TD([[subQ7,-1.0]])],"derivedFrom":subQ5}),1.0]])]});}
            var Q39;
            {var subQ5=sQuery(id+"F1.wireOp",EDGE,"E35.1.endCap");Q39=makeQuery(id+"F1.imprint","IMPRINT",FACE,{"disambiguationData":[TD([[makeQuery(id+"F1.imprint","IMPRINT",EDGE,{"derivedFrom":subQ5}),1.0]])]});}
            var Q40;
            {var subQ0=sQuery(id+"F1.wireOp",EDGE,"E35.0.endCap");var subQ5=sQuery(id+"F1.wireOp",EDGE,"E35.2.left");var subQ7=makeQuery(id+"F1.imprint","INTERSECT",VERTEX,{"derivedFrom":[subQ0,subQ5]});Q40=makeQuery(id+"F1.imprint","IMPRINT",FACE,{"disambiguationData":[TD([[makeQuery(id+"F1.imprint","IMPRINT",EDGE,{"disambiguationData":[TD([[subQ7,1.0]])],"derivedFrom":subQ5}),-1.0]])]});}
            var Q41;
            {var subQ3=sQuery(id+"F1.wireOp",EDGE,"E35.1.startCap");Q41=makeQuery(id+"F1.imprint","IMPRINT",FACE,{"disambiguationData":[TD([[makeQuery(id+"F1.imprint","IMPRINT",EDGE,{"derivedFrom":subQ3}),1.0]])]});}
            var Q42;
            {var subQ1=sQuery(id+"F1.wireOp",EDGE,"11422904-8dbc-437f-b2cb-607545d81d6e.0");var subQ3=sQuery(id+"F1.wireOp",EDGE,"52e85f9d-6710-4ef4-a348-8d421ddb169b.0.startCap");var subQ4=makeQuery(id+"F1.imprint","INTERSECT",VERTEX,{"derivedFrom":[subQ1,subQ3]});Q42=makeQuery(id+"F1.imprint","IMPRINT",FACE,{"disambiguationData":[TD([[makeQuery(id+"F1.imprint","IMPRINT",EDGE,{"disambiguationData":[TD([[subQ4,-1.0]])],"derivedFrom":subQ1}),1.0]])]});}
            var Q43;
            {var subQ3=sQuery(id+"F1.wireOp",EDGE,"E35.8.endCap");var subQ5=sQuery(id+"F1.wireOp",EDGE,"E35.2.left");var subQ7=makeQuery(id+"F1.imprint","INTERSECT",VERTEX,{"derivedFrom":[subQ5,subQ3]});Q43=makeQuery(id+"F1.imprint","IMPRINT",FACE,{"disambiguationData":[TD([[makeQuery(id+"F1.imprint","IMPRINT",EDGE,{"disambiguationData":[TD([[subQ7,1.0]])],"derivedFrom":subQ5}),-1.0]])]});}
            var Q44;
            {var subQ3=sQuery(id+"F1.wireOp",EDGE,"E35.8.endCap");var subQ5=sQuery(id+"F1.wireOp",EDGE,"E35.2.left");var subQ6=makeQuery(id+"F1.imprint","INTERSECT",VERTEX,{"derivedFrom":[subQ5,subQ3]});Q44=makeQuery(id+"F1.imprint","IMPRINT",FACE,{"disambiguationData":[TD([[makeQuery(id+"F1.imprint","IMPRINT",EDGE,{"disambiguationData":[TD([[subQ6,-1.0]])],"derivedFrom":subQ5}),-1.0]])]});}
            var Q45;
            {var subQ3=sQuery(id+"F1.wireOp",EDGE,"E35.7.startCap");var subQ5=sQuery(id+"F1.wireOp",EDGE,"E35.2.left");var subQ6=makeQuery(id+"F1.imprint","INTERSECT",VERTEX,{"derivedFrom":[subQ5,subQ3]});Q45=makeQuery(id+"F1.imprint","IMPRINT",FACE,{"disambiguationData":[TD([[makeQuery(id+"F1.imprint","IMPRINT",EDGE,{"disambiguationData":[TD([[subQ6,-1.0]])],"derivedFrom":subQ5}),-1.0]])]});}
            var Q46;
            {var subQ3=sQuery(id+"F1.wireOp",EDGE,"E35.5.right");var subQ5=sQuery(id+"F1.wireOp",EDGE,"E35.2.right");var subQ6=makeQuery(id+"F1.imprint","INTERSECT",VERTEX,{"derivedFrom":[subQ5,subQ3]});Q46=makeQuery(id+"F1.imprint","IMPRINT",FACE,{"disambiguationData":[TD([[makeQuery(id+"F1.imprint","IMPRINT",EDGE,{"disambiguationData":[TD([[subQ6,-1.0]])],"derivedFrom":subQ5}),1.0]])]});}
            var Q47;
            {var subQ1=sQuery(id+"F1.wireOp",EDGE,"E35.4.startCap");var subQ3=sQuery(id+"F1.wireOp",EDGE,"52e85f9d-6710-4ef4-a348-8d421ddb169b.0.right");var subQ4=makeQuery(id+"F1.imprint","INTERSECT",VERTEX,{"derivedFrom":[subQ1,subQ3]});Q47=makeQuery(id+"F1.imprint","IMPRINT",FACE,{"disambiguationData":[TD([[makeQuery(id+"F1.imprint","IMPRINT",EDGE,{"disambiguationData":[TD([[subQ4,-1.0]])],"derivedFrom":subQ3}),1.0]])]});}
            var Q48;
            {var subQ0=sQuery(id+"F1.wireOp",EDGE,"E35.4.endCap");var subQ5=sQuery(id+"F1.wireOp",EDGE,"E35.2.left");var subQ6=makeQuery(id+"F1.imprint","INTERSECT",VERTEX,{"derivedFrom":[subQ5,subQ0]});Q48=makeQuery(id+"F1.imprint","IMPRINT",FACE,{"disambiguationData":[TD([[makeQuery(id+"F1.imprint","IMPRINT",EDGE,{"disambiguationData":[TD([[subQ6,-1.0]])],"derivedFrom":subQ5}),-1.0]])]});}
            var Q49;
            {var subQ3=sQuery(id+"F1.wireOp",EDGE,"E35.5.endCap");var subQ5=sQuery(id+"F1.wireOp",EDGE,"E35.2.left");var subQ7=makeQuery(id+"F1.imprint","INTERSECT",VERTEX,{"derivedFrom":[subQ5,subQ3]});Q49=makeQuery(id+"F1.imprint","IMPRINT",FACE,{"disambiguationData":[TD([[makeQuery(id+"F1.imprint","IMPRINT",EDGE,{"disambiguationData":[TD([[subQ7,-1.0]])],"derivedFrom":subQ5}),-1.0]])]});}
            var Q50;
            {var subQ3=sQuery(id+"F1.wireOp",EDGE,"E35.8.right");var subQ5=sQuery(id+"F1.wireOp",EDGE,"E35.2.right");var subQ6=makeQuery(id+"F1.imprint","INTERSECT",VERTEX,{"derivedFrom":[subQ5,subQ3]});Q50=makeQuery(id+"F1.imprint","IMPRINT",FACE,{"disambiguationData":[TD([[makeQuery(id+"F1.imprint","IMPRINT",EDGE,{"disambiguationData":[TD([[subQ6,-1.0]])],"derivedFrom":subQ5}),1.0]])]});}
            var Q51;
            {var subQ0=sQuery(id+"F1.wireOp",EDGE,"11422904-8dbc-437f-b2cb-607545d81d6e.0");var subQ1=sQuery(id+"F1.wireOp",EDGE,"E29.0");var subQ2=makeQuery(id+"F1.imprint","INTERSECT",VERTEX,{"derivedFrom":[subQ1,subQ0]});Q51=makeQuery(id+"F1.imprint","IMPRINT",FACE,{"disambiguationData":[TD([[makeQuery(id+"F1.imprint","IMPRINT",EDGE,{"disambiguationData":[TD([[subQ2,1.0]])],"derivedFrom":subQ1}),-1.0]])]});}
            var Q52;
            {var subQ0=sQuery(id+"F1.wireOp",EDGE,"11422904-8dbc-437f-b2cb-607545d81d6e.0");var subQ1=sQuery(id+"F1.wireOp",EDGE,"E31.0");var subQ2=makeQuery(id+"F1.imprint","INTERSECT",VERTEX,{"derivedFrom":[subQ1,subQ0]});Q52=makeQuery(id+"F1.imprint","IMPRINT",FACE,{"disambiguationData":[TD([[makeQuery(id+"F1.imprint","IMPRINT",EDGE,{"disambiguationData":[TD([[subQ2,1.0]])],"derivedFrom":subQ1}),-1.0]])]});}
            var Q53;
            {var subQ0=sQuery(id+"F1.wireOp",EDGE,"11422904-8dbc-437f-b2cb-607545d81d6e.0");var subQ1=makeQuery(id+"F1.imprint","INTERSECT",VERTEX,{"derivedFrom":[sQuery(id+"F1.wireOp",EDGE,"E31.0"),subQ0]});Q53=makeQuery(id+"F1.imprint","IMPRINT",FACE,{"disambiguationData":[TD([[makeQuery(id+"F1.imprint","IMPRINT",EDGE,{"disambiguationData":[TD([[subQ1,1.0]])],"derivedFrom":subQ0}),1.0]])]});}
            var Q54;
            {var subQ0=sQuery(id+"F1.wireOp",EDGE,"11422904-8dbc-437f-b2cb-607545d81d6e.0");var subQ1=sQuery(id+"F1.wireOp",EDGE,"E29.0");var subQ2=makeQuery(id+"F1.imprint","INTERSECT",VERTEX,{"derivedFrom":[subQ1,subQ0]});Q54=makeQuery(id+"F1.imprint","IMPRINT",FACE,{"disambiguationData":[TD([[makeQuery(id+"F1.imprint","IMPRINT",EDGE,{"disambiguationData":[TD([[subQ2,1.0]])],"derivedFrom":subQ1}),1.0]])]});}
            var Q55;
            {var subQ0=sQuery(id+"F1.wireOp",EDGE,"11422904-8dbc-437f-b2cb-607545d81d6e.0");var subQ1=sQuery(id+"F1.wireOp",EDGE,"E31.0");var subQ2=makeQuery(id+"F1.imprint","INTERSECT",VERTEX,{"derivedFrom":[subQ1,subQ0]});Q55=makeQuery(id+"F1.imprint","IMPRINT",FACE,{"disambiguationData":[TD([[makeQuery(id+"F1.imprint","IMPRINT",EDGE,{"disambiguationData":[TD([[subQ2,1.0]])],"derivedFrom":subQ1}),1.0]])]});}
            var Q56;
            {var subQ1=sQuery(id+"F1.wireOp",EDGE,"E35.3.right");var subQ3=sQuery(id+"F1.wireOp",EDGE,"52e85f9d-6710-4ef4-a348-8d421ddb169b.0.left");var subQ4=makeQuery(id+"F1.imprint","INTERSECT",VERTEX,{"derivedFrom":[subQ1,subQ3]});Q56=makeQuery(id+"F1.imprint","IMPRINT",FACE,{"disambiguationData":[TD([[makeQuery(id+"F1.imprint","IMPRINT",EDGE,{"disambiguationData":[TD([[subQ4,1.0]])],"derivedFrom":subQ3}),-1.0]])]});}
            var Q57;
            {var subQ0=sQuery(id+"F1.wireOp",EDGE,"e885aaa4-3fd3-4c22-b075-bbe01348cefd0.MirrorCS");var subQ1=sQuery(id+"F1.wireOp",EDGE,"E31.0");var subQ2=makeQuery(id+"F1.imprint","INTERSECT",VERTEX,{"derivedFrom":[subQ1,subQ0]});Q57=makeQuery(id+"F1.imprint","IMPRINT",FACE,{"disambiguationData":[TD([[makeQuery(id+"F1.imprint","IMPRINT",EDGE,{"disambiguationData":[TD([[subQ2,-1.0]])],"derivedFrom":subQ1}),1.0]])]});}
            var Q58;
            {var subQ0=sQuery(id+"F1.wireOp",EDGE,"11422904-8dbc-437f-b2cb-607545d81d6e.0");var subQ1=sQuery(id+"F1.wireOp",EDGE,"E32.0");var subQ2=makeQuery(id+"F1.imprint","INTERSECT",VERTEX,{"derivedFrom":[subQ1,subQ0]});Q58=makeQuery(id+"F1.imprint","IMPRINT",FACE,{"disambiguationData":[TD([[makeQuery(id+"F1.imprint","IMPRINT",EDGE,{"disambiguationData":[TD([[subQ2,-1.0]])],"derivedFrom":subQ1}),-1.0]])]});}
            var Q59;
            {var subQ0=sQuery(id+"F1.wireOp",EDGE,"11422904-8dbc-437f-b2cb-607545d81d6e.0");var subQ1=sQuery(id+"F1.wireOp",EDGE,"E33.0");var subQ2=makeQuery(id+"F1.imprint","INTERSECT",VERTEX,{"derivedFrom":[subQ1,subQ0]});Q59=makeQuery(id+"F1.imprint","IMPRINT",FACE,{"disambiguationData":[TD([[makeQuery(id+"F1.imprint","IMPRINT",EDGE,{"disambiguationData":[TD([[subQ2,1.0]])],"derivedFrom":subQ1}),1.0]])]});}
            var Q60;
            {var subQ0=sQuery(id+"F1.wireOp",EDGE,"11422904-8dbc-437f-b2cb-607545d81d6e.0");var subQ1=sQuery(id+"F1.wireOp",EDGE,"E32.0");var subQ2=makeQuery(id+"F1.imprint","INTERSECT",VERTEX,{"derivedFrom":[subQ1,subQ0]});Q60=makeQuery(id+"F1.imprint","IMPRINT",FACE,{"disambiguationData":[TD([[makeQuery(id+"F1.imprint","IMPRINT",EDGE,{"disambiguationData":[TD([[subQ2,-1.0]])],"derivedFrom":subQ1}),1.0]])]});}
            var Q61;
            {var subQ0=sQuery(id+"F1.wireOp",EDGE,"11422904-8dbc-437f-b2cb-607545d81d6e.0");var subQ1=sQuery(id+"F1.wireOp",EDGE,"E30.0");var subQ2=makeQuery(id+"F1.imprint","INTERSECT",VERTEX,{"derivedFrom":[subQ1,subQ0]});Q61=makeQuery(id+"F1.imprint","IMPRINT",FACE,{"disambiguationData":[TD([[makeQuery(id+"F1.imprint","IMPRINT",EDGE,{"disambiguationData":[TD([[subQ2,-1.0]])],"derivedFrom":subQ1}),1.0]])]});}
            var Q62;
            {var subQ0=sQuery(id+"F1.wireOp",EDGE,"11422904-8dbc-437f-b2cb-607545d81d6e.0");var subQ1=makeQuery(id+"F1.imprint","INTERSECT",VERTEX,{"derivedFrom":[sQuery(id+"F1.wireOp",EDGE,"E29.0"),subQ0]});Q62=makeQuery(id+"F1.imprint","IMPRINT",FACE,{"disambiguationData":[TD([[makeQuery(id+"F1.imprint","IMPRINT",EDGE,{"disambiguationData":[TD([[subQ1,1.0]])],"derivedFrom":subQ0}),1.0]])]});}
            var Q63;
            {var subQ0=sQuery(id+"F1.wireOp",EDGE,"11422904-8dbc-437f-b2cb-607545d81d6e.0");var subQ1=sQuery(id+"F1.wireOp",EDGE,"E34.0");var subQ2=makeQuery(id+"F1.imprint","INTERSECT",VERTEX,{"derivedFrom":[subQ1,subQ0]});Q63=makeQuery(id+"F1.imprint","IMPRINT",FACE,{"disambiguationData":[TD([[makeQuery(id+"F1.imprint","IMPRINT",EDGE,{"disambiguationData":[TD([[subQ2,-1.0]])],"derivedFrom":subQ1}),-1.0]])]});}
            var Q64;
            {var subQ0=sQuery(id+"F1.wireOp",EDGE,"11422904-8dbc-437f-b2cb-607545d81d6e.0");var subQ1=sQuery(id+"F1.wireOp",EDGE,"E33.0");var subQ2=makeQuery(id+"F1.imprint","INTERSECT",VERTEX,{"derivedFrom":[subQ1,subQ0]});Q64=makeQuery(id+"F1.imprint","IMPRINT",FACE,{"disambiguationData":[TD([[makeQuery(id+"F1.imprint","IMPRINT",EDGE,{"disambiguationData":[TD([[subQ2,1.0]])],"derivedFrom":subQ1}),1.0]])]});}
            var Q65;
            {var subQ0=sQuery(id+"F1.wireOp",EDGE,"e885aaa4-3fd3-4c22-b075-bbe01348cefd0.MirrorCS");var subQ1=sQuery(id+"F1.wireOp",EDGE,"E29.0");var subQ2=makeQuery(id+"F1.imprint","INTERSECT",VERTEX,{"derivedFrom":[subQ1,subQ0]});Q65=makeQuery(id+"F1.imprint","IMPRINT",FACE,{"disambiguationData":[TD([[makeQuery(id+"F1.imprint","IMPRINT",EDGE,{"disambiguationData":[TD([[subQ2,-1.0]])],"derivedFrom":subQ1}),1.0]])]});}
            var Q66;
            {var subQ0=sQuery(id+"F1.wireOp",EDGE,"11422904-8dbc-437f-b2cb-607545d81d6e.0");var subQ1=makeQuery(id+"F1.imprint","INTERSECT",VERTEX,{"derivedFrom":[sQuery(id+"F1.wireOp",EDGE,"E30.0"),subQ0]});Q66=makeQuery(id+"F1.imprint","IMPRINT",FACE,{"disambiguationData":[TD([[makeQuery(id+"F1.imprint","IMPRINT",EDGE,{"disambiguationData":[TD([[subQ1,1.0]])],"derivedFrom":subQ0}),1.0]])]});}
            var Q67;
            {var subQ0=sQuery(id+"F1.wireOp",EDGE,"11422904-8dbc-437f-b2cb-607545d81d6e.0");var subQ1=makeQuery(id+"F1.imprint","INTERSECT",VERTEX,{"derivedFrom":[sQuery(id+"F1.wireOp",EDGE,"E34.0"),subQ0]});Q67=makeQuery(id+"F1.imprint","IMPRINT",FACE,{"disambiguationData":[TD([[makeQuery(id+"F1.imprint","IMPRINT",EDGE,{"disambiguationData":[TD([[subQ1,1.0]])],"derivedFrom":subQ0}),1.0]])]});}
            var Q68;
            {var subQ0=sQuery(id+"F1.wireOp",EDGE,"11422904-8dbc-437f-b2cb-607545d81d6e.0");var subQ1=sQuery(id+"F1.wireOp",EDGE,"E33.0");var subQ2=makeQuery(id+"F1.imprint","INTERSECT",VERTEX,{"derivedFrom":[subQ1,subQ0]});Q68=makeQuery(id+"F1.imprint","IMPRINT",FACE,{"disambiguationData":[TD([[makeQuery(id+"F1.imprint","IMPRINT",EDGE,{"disambiguationData":[TD([[subQ2,1.0]])],"derivedFrom":subQ1}),-1.0]])]});}
            var Q69;
            {var subQ0=sQuery(id+"F1.wireOp",EDGE,"e885aaa4-3fd3-4c22-b075-bbe01348cefd0.MirrorCS");var subQ1=sQuery(id+"F1.wireOp",EDGE,"E31.0");var subQ2=makeQuery(id+"F1.imprint","INTERSECT",VERTEX,{"derivedFrom":[subQ1,subQ0]});Q69=makeQuery(id+"F1.imprint","IMPRINT",FACE,{"disambiguationData":[TD([[makeQuery(id+"F1.imprint","IMPRINT",EDGE,{"disambiguationData":[TD([[subQ2,-1.0]])],"derivedFrom":subQ1}),-1.0]])]});}
            var Q70;
            {var subQ0=sQuery(id+"F1.wireOp",EDGE,"e885aaa4-3fd3-4c22-b075-bbe01348cefd0.MirrorCS");var subQ1=sQuery(id+"F1.wireOp",EDGE,"E33.0");var subQ2=makeQuery(id+"F1.imprint","INTERSECT",VERTEX,{"derivedFrom":[subQ1,subQ0]});Q70=makeQuery(id+"F1.imprint","IMPRINT",FACE,{"disambiguationData":[TD([[makeQuery(id+"F1.imprint","IMPRINT",EDGE,{"disambiguationData":[TD([[subQ2,-1.0]])],"derivedFrom":subQ1}),1.0]])]});}
            var Q71;
            {var subQ0=sQuery(id+"F1.wireOp",EDGE,"11422904-8dbc-437f-b2cb-607545d81d6e.0");var subQ1=makeQuery(id+"F1.imprint","INTERSECT",VERTEX,{"derivedFrom":[sQuery(id+"F1.wireOp",EDGE,"E33.0"),subQ0]});Q71=makeQuery(id+"F1.imprint","IMPRINT",FACE,{"disambiguationData":[TD([[makeQuery(id+"F1.imprint","IMPRINT",EDGE,{"disambiguationData":[TD([[subQ1,1.0]])],"derivedFrom":subQ0}),1.0]])]});}
            var Q72;
            {var subQ0=sQuery(id+"F1.wireOp",EDGE,"11422904-8dbc-437f-b2cb-607545d81d6e.0");var subQ1=sQuery(id+"F1.wireOp",EDGE,"E34.0");var subQ2=makeQuery(id+"F1.imprint","INTERSECT",VERTEX,{"derivedFrom":[subQ1,subQ0]});Q72=makeQuery(id+"F1.imprint","IMPRINT",FACE,{"disambiguationData":[TD([[makeQuery(id+"F1.imprint","IMPRINT",EDGE,{"disambiguationData":[TD([[subQ2,-1.0]])],"derivedFrom":subQ1}),1.0]])]});}
            var Q73;
            {var subQ1=sQuery(id+"F1.wireOp",EDGE,"E35.0.startCap");var subQ3=makeQuery(id+"F1.imprint","INTERSECT",VERTEX,{"derivedFrom":[subQ1,sQuery(id+"F1.wireOp",EDGE,"52e85f9d-6710-4ef4-a348-8d421ddb169b.0.right")]});Q73=makeQuery(id+"F1.imprint","IMPRINT",FACE,{"disambiguationData":[TD([[makeQuery(id+"F1.imprint","IMPRINT",EDGE,{"disambiguationData":[TD([[subQ3,1.0]])],"derivedFrom":subQ1}),-1.0]])]});}
            var Q74;
            {var subQ0=sQuery(id+"F1.wireOp",EDGE,"11422904-8dbc-437f-b2cb-607545d81d6e.0");var subQ1=sQuery(id+"F1.wireOp",EDGE,"E33.0");var subQ2=makeQuery(id+"F1.imprint","INTERSECT",VERTEX,{"derivedFrom":[subQ1,subQ0]});Q74=makeQuery(id+"F1.imprint","IMPRINT",FACE,{"disambiguationData":[TD([[makeQuery(id+"F1.imprint","IMPRINT",EDGE,{"disambiguationData":[TD([[subQ2,1.0]])],"derivedFrom":subQ1}),-1.0]])]});}
            var Q75;
            {var subQ0=sQuery(id+"F1.wireOp",EDGE,"11422904-8dbc-437f-b2cb-607545d81d6e.0");var subQ1=makeQuery(id+"F1.imprint","INTERSECT",VERTEX,{"derivedFrom":[sQuery(id+"F1.wireOp",EDGE,"E33.0"),subQ0]});Q75=makeQuery(id+"F1.imprint","IMPRINT",FACE,{"disambiguationData":[TD([[makeQuery(id+"F1.imprint","IMPRINT",EDGE,{"disambiguationData":[TD([[subQ1,1.0]])],"derivedFrom":subQ0}),1.0]])]});}
            var Q76;
            {var subQ0=sQuery(id+"F1.wireOp",EDGE,"e885aaa4-3fd3-4c22-b075-bbe01348cefd0.MirrorCS");var subQ1=sQuery(id+"F1.wireOp",EDGE,"E33.0");var subQ2=makeQuery(id+"F1.imprint","INTERSECT",VERTEX,{"derivedFrom":[subQ1,subQ0]});Q76=makeQuery(id+"F1.imprint","IMPRINT",FACE,{"disambiguationData":[TD([[makeQuery(id+"F1.imprint","IMPRINT",EDGE,{"disambiguationData":[TD([[subQ2,-1.0]])],"derivedFrom":subQ1}),1.0]])]});}
            var Q77;
            {var subQ0=sQuery(id+"F1.wireOp",EDGE,"11422904-8dbc-437f-b2cb-607545d81d6e.0");var subQ1=sQuery(id+"F1.wireOp",EDGE,"E30.0");var subQ2=makeQuery(id+"F1.imprint","INTERSECT",VERTEX,{"derivedFrom":[subQ1,subQ0]});Q77=makeQuery(id+"F1.imprint","IMPRINT",FACE,{"disambiguationData":[TD([[makeQuery(id+"F1.imprint","IMPRINT",EDGE,{"disambiguationData":[TD([[subQ2,-1.0]])],"derivedFrom":subQ1}),-1.0]])]});}
            var Q78;
            {var subQ0=sQuery(id+"F1.wireOp",EDGE,"e885aaa4-3fd3-4c22-b075-bbe01348cefd0.MirrorCS");var subQ1=sQuery(id+"F1.wireOp",EDGE,"E29.0");var subQ2=makeQuery(id+"F1.imprint","INTERSECT",VERTEX,{"derivedFrom":[subQ1,subQ0]});Q78=makeQuery(id+"F1.imprint","IMPRINT",FACE,{"disambiguationData":[TD([[makeQuery(id+"F1.imprint","IMPRINT",EDGE,{"disambiguationData":[TD([[subQ2,-1.0]])],"derivedFrom":subQ1}),-1.0]])]});}
            var Q79;
            {var subQ0=sQuery(id+"F1.wireOp",EDGE,"11422904-8dbc-437f-b2cb-607545d81d6e.0");var subQ1=makeQuery(id+"F1.imprint","INTERSECT",VERTEX,{"derivedFrom":[sQuery(id+"F1.wireOp",EDGE,"E32.0"),subQ0]});Q79=makeQuery(id+"F1.imprint","IMPRINT",FACE,{"disambiguationData":[TD([[makeQuery(id+"F1.imprint","IMPRINT",EDGE,{"disambiguationData":[TD([[subQ1,1.0]])],"derivedFrom":subQ0}),1.0]])]});}
            var Q80;
            {var subQ0=sQuery(id+"F1.wireOp",EDGE,"e885aaa4-3fd3-4c22-b075-bbe01348cefd0.MirrorCS");var subQ1=sQuery(id+"F1.wireOp",EDGE,"E33.0");var subQ2=makeQuery(id+"F1.imprint","INTERSECT",VERTEX,{"derivedFrom":[subQ1,subQ0]});Q80=makeQuery(id+"F1.imprint","IMPRINT",FACE,{"disambiguationData":[TD([[makeQuery(id+"F1.imprint","IMPRINT",EDGE,{"disambiguationData":[TD([[subQ2,-1.0]])],"derivedFrom":subQ1}),-1.0]])]});}
            var Q81;
            {var subQ1=sQuery(id+"F1.wireOp",EDGE,"E35.8.startCap");var subQ3=makeQuery(id+"F1.imprint","INTERSECT",VERTEX,{"derivedFrom":[subQ1,sQuery(id+"F1.wireOp",EDGE,"52e85f9d-6710-4ef4-a348-8d421ddb169b.0.right")]});Q81=makeQuery(id+"F1.imprint","IMPRINT",FACE,{"disambiguationData":[TD([[makeQuery(id+"F1.imprint","IMPRINT",EDGE,{"disambiguationData":[TD([[subQ3,1.0]])],"derivedFrom":subQ1}),-1.0]])]});}
            var Q82;
            {var subQ1=sQuery(id+"F1.wireOp",EDGE,"E35.5.startCap");var subQ3=makeQuery(id+"F1.imprint","INTERSECT",VERTEX,{"derivedFrom":[subQ1,sQuery(id+"F1.wireOp",EDGE,"52e85f9d-6710-4ef4-a348-8d421ddb169b.0.right")]});Q82=makeQuery(id+"F1.imprint","IMPRINT",FACE,{"disambiguationData":[TD([[makeQuery(id+"F1.imprint","IMPRINT",EDGE,{"disambiguationData":[TD([[subQ3,1.0]])],"derivedFrom":subQ1}),-1.0]])]});}
            var Q83;
            {var subQ0=sQuery(id+"F1.wireOp",EDGE,"e885aaa4-3fd3-4c22-b075-bbe01348cefd0.MirrorCS");var subQ1=sQuery(id+"F1.wireOp",EDGE,"E33.0");var subQ2=makeQuery(id+"F1.imprint","INTERSECT",VERTEX,{"derivedFrom":[subQ1,subQ0]});Q83=makeQuery(id+"F1.imprint","IMPRINT",FACE,{"disambiguationData":[TD([[makeQuery(id+"F1.imprint","IMPRINT",EDGE,{"disambiguationData":[TD([[subQ2,-1.0]])],"derivedFrom":subQ1}),-1.0]])]});}
            var Q84;
            {var subQ0=sQuery(id+"F1.wireOp",EDGE,"e885aaa4-3fd3-4c22-b075-bbe01348cefd0.MirrorCS");var subQ1=sQuery(id+"F1.wireOp",EDGE,"E30.0");var subQ2=makeQuery(id+"F1.imprint","INTERSECT",VERTEX,{"derivedFrom":[subQ1,subQ0]});Q84=makeQuery(id+"F1.imprint","IMPRINT",FACE,{"disambiguationData":[TD([[makeQuery(id+"F1.imprint","IMPRINT",EDGE,{"disambiguationData":[TD([[subQ2,1.0]])],"derivedFrom":subQ1}),-1.0]])]});}
            var Q85;
            {var subQ1=sQuery(id+"F1.wireOp",EDGE,"E35.4.startCap");var subQ3=makeQuery(id+"F1.imprint","INTERSECT",VERTEX,{"derivedFrom":[subQ1,sQuery(id+"F1.wireOp",EDGE,"52e85f9d-6710-4ef4-a348-8d421ddb169b.0.right")]});Q85=makeQuery(id+"F1.imprint","IMPRINT",FACE,{"disambiguationData":[TD([[makeQuery(id+"F1.imprint","IMPRINT",EDGE,{"disambiguationData":[TD([[subQ3,1.0]])],"derivedFrom":subQ1}),-1.0]])]});}
            var Q86;
            {var subQ1=sQuery(id+"F1.wireOp",EDGE,"E35.3.endCap");var subQ3=sQuery(id+"F1.wireOp",EDGE,"52e85f9d-6710-4ef4-a348-8d421ddb169b.0.right");var subQ4=makeQuery(id+"F1.imprint","INTERSECT",VERTEX,{"derivedFrom":[subQ1,subQ3]});Q86=makeQuery(id+"F1.imprint","IMPRINT",FACE,{"disambiguationData":[TD([[makeQuery(id+"F1.imprint","IMPRINT",EDGE,{"disambiguationData":[TD([[subQ4,1.0]])],"derivedFrom":subQ3}),1.0]])]});}
            var Q87;
            {var subQ0=sQuery(id+"F1.wireOp",EDGE,"e885aaa4-3fd3-4c22-b075-bbe01348cefd0.MirrorCS");var subQ1=sQuery(id+"F1.wireOp",EDGE,"E34.0");var subQ2=makeQuery(id+"F1.imprint","INTERSECT",VERTEX,{"derivedFrom":[subQ1,subQ0]});Q87=makeQuery(id+"F1.imprint","IMPRINT",FACE,{"disambiguationData":[TD([[makeQuery(id+"F1.imprint","IMPRINT",EDGE,{"disambiguationData":[TD([[subQ2,1.0]])],"derivedFrom":subQ1}),1.0]])]});}
            var Q88;
            {var subQ0=sQuery(id+"F1.wireOp",EDGE,"e885aaa4-3fd3-4c22-b075-bbe01348cefd0.MirrorCS");var subQ1=sQuery(id+"F1.wireOp",EDGE,"E32.0");var subQ2=makeQuery(id+"F1.imprint","INTERSECT",VERTEX,{"derivedFrom":[subQ1,subQ0]});Q88=makeQuery(id+"F1.imprint","IMPRINT",FACE,{"disambiguationData":[TD([[makeQuery(id+"F1.imprint","IMPRINT",EDGE,{"disambiguationData":[TD([[subQ2,1.0]])],"derivedFrom":subQ1}),-1.0]])]});}
            var Q89;
            {var subQ1=sQuery(id+"F1.wireOp",EDGE,"E35.3.endCap");var subQ3=makeQuery(id+"F1.imprint","INTERSECT",VERTEX,{"derivedFrom":[subQ1,sQuery(id+"F1.wireOp",EDGE,"52e85f9d-6710-4ef4-a348-8d421ddb169b.0.right")]});Q89=makeQuery(id+"F1.imprint","IMPRINT",FACE,{"disambiguationData":[TD([[makeQuery(id+"F1.imprint","IMPRINT",EDGE,{"disambiguationData":[TD([[subQ3,1.0]])],"derivedFrom":subQ1}),-1.0]])]});}
            var Q90;
            {var subQ0=sQuery(id+"F1.wireOp",EDGE,"e885aaa4-3fd3-4c22-b075-bbe01348cefd0.MirrorCS");var subQ1=sQuery(id+"F1.wireOp",EDGE,"E30.0");var subQ2=makeQuery(id+"F1.imprint","INTERSECT",VERTEX,{"derivedFrom":[subQ1,subQ0]});Q90=makeQuery(id+"F1.imprint","IMPRINT",FACE,{"disambiguationData":[TD([[makeQuery(id+"F1.imprint","IMPRINT",EDGE,{"disambiguationData":[TD([[subQ2,1.0]])],"derivedFrom":subQ1}),1.0]])]});}
            var Q91;
            {var subQ1=sQuery(id+"F1.wireOp",EDGE,"E35.7.endCap");var subQ3=makeQuery(id+"F1.imprint","INTERSECT",VERTEX,{"derivedFrom":[subQ1,sQuery(id+"F1.wireOp",EDGE,"52e85f9d-6710-4ef4-a348-8d421ddb169b.0.right")]});Q91=makeQuery(id+"F1.imprint","IMPRINT",FACE,{"disambiguationData":[TD([[makeQuery(id+"F1.imprint","IMPRINT",EDGE,{"disambiguationData":[TD([[subQ3,1.0]])],"derivedFrom":subQ1}),-1.0]])]});}
            var Q92;
            {var subQ0=sQuery(id+"F1.wireOp",EDGE,"e885aaa4-3fd3-4c22-b075-bbe01348cefd0.MirrorCS");var subQ1=sQuery(id+"F1.wireOp",EDGE,"E34.0");var subQ2=makeQuery(id+"F1.imprint","INTERSECT",VERTEX,{"derivedFrom":[subQ1,subQ0]});Q92=makeQuery(id+"F1.imprint","IMPRINT",FACE,{"disambiguationData":[TD([[makeQuery(id+"F1.imprint","IMPRINT",EDGE,{"disambiguationData":[TD([[subQ2,1.0]])],"derivedFrom":subQ1}),-1.0]])]});}
            var Q93;
            {var subQ0=sQuery(id+"F1.wireOp",EDGE,"e885aaa4-3fd3-4c22-b075-bbe01348cefd0.MirrorCS");var subQ1=sQuery(id+"F1.wireOp",EDGE,"E32.0");var subQ2=makeQuery(id+"F1.imprint","INTERSECT",VERTEX,{"derivedFrom":[subQ1,subQ0]});Q93=makeQuery(id+"F1.imprint","IMPRINT",FACE,{"disambiguationData":[TD([[makeQuery(id+"F1.imprint","IMPRINT",EDGE,{"disambiguationData":[TD([[subQ2,1.0]])],"derivedFrom":subQ1}),1.0]])]});}
            var Q94;
            {var subQ1=sQuery(id+"F1.wireOp",EDGE,"E35.6.endCap");var subQ3=makeQuery(id+"F1.imprint","INTERSECT",VERTEX,{"derivedFrom":[subQ1,sQuery(id+"F1.wireOp",EDGE,"52e85f9d-6710-4ef4-a348-8d421ddb169b.0.right")]});Q94=makeQuery(id+"F1.imprint","IMPRINT",FACE,{"disambiguationData":[TD([[makeQuery(id+"F1.imprint","IMPRINT",EDGE,{"disambiguationData":[TD([[subQ3,1.0]])],"derivedFrom":subQ1}),-1.0]])]});}
            var Q95;
            {var subQ0=sQuery(id+"F1.wireOp",EDGE,"11422904-8dbc-437f-b2cb-607545d81d6e.0");var subQ1=sQuery(id+"F1.wireOp",EDGE,"d5c510f4-37f1-434f-946f-66e03c4c81df.0");var subQ2=makeQuery(id+"F1.imprint","INTERSECT",VERTEX,{"derivedFrom":[subQ1,subQ0]});Q95=makeQuery(id+"F1.imprint","IMPRINT",FACE,{"disambiguationData":[TD([[makeQuery(id+"F1.imprint","IMPRINT",EDGE,{"disambiguationData":[TD([[subQ2,-1.0]])],"derivedFrom":subQ1}),-1.0]])]});}
            var Q96;
            {var subQ7=sQuery(id+"F1.wireOp",EDGE,"E35.1.endCap");Q96=makeQuery(id+"F1.imprint","IMPRINT",FACE,{"disambiguationData":[TD([[makeQuery(id+"F1.imprint","IMPRINT",EDGE,{"derivedFrom":subQ7}),-1.0]])]});}
            var Q97;
            {var subQ0=sQuery(id+"F1.wireOp",EDGE,"e885aaa4-3fd3-4c22-b075-bbe01348cefd0.MirrorCS");var subQ1=sQuery(id+"F1.wireOp",EDGE,"d5c510f4-37f1-434f-946f-66e03c4c81df.0");var subQ2=makeQuery(id+"F1.imprint","INTERSECT",VERTEX,{"derivedFrom":[subQ1,subQ0]});Q97=makeQuery(id+"F1.imprint","IMPRINT",FACE,{"disambiguationData":[TD([[makeQuery(id+"F1.imprint","IMPRINT",EDGE,{"disambiguationData":[TD([[subQ2,1.0]])],"derivedFrom":subQ1}),-1.0]])]});}
            var Q98;
            {var subQ1=sQuery(id+"F1.wireOp",EDGE,"E35.1.startCap");Q98=makeQuery(id+"F1.imprint","IMPRINT",FACE,{"disambiguationData":[TD([[makeQuery(id+"F1.imprint","IMPRINT",EDGE,{"derivedFrom":subQ1}),-1.0]])]});}
            var Q99;
            {var subQ0=sQuery(id+"F1.wireOp",EDGE,"e885aaa4-3fd3-4c22-b075-bbe01348cefd0.MirrorCS");var subQ1=sQuery(id+"F1.wireOp",EDGE,"11422904-8dbc-437f-b2cb-607545d81d6e.0");var subQ2=makeQuery(id+"F1.imprint","INTERSECT",VERTEX,{"derivedFrom":[subQ1,subQ0]});Q99=makeQuery(id+"F1.imprint","IMPRINT",FACE,{"disambiguationData":[TD([[makeQuery(id+"F1.imprint","IMPRINT",EDGE,{"disambiguationData":[TD([[subQ2,-1.0]])],"derivedFrom":subQ1}),-1.0]])]});}
            var Q100;
            {var subQ0=sQuery(id+"F1.wireOp",EDGE,"e885aaa4-3fd3-4c22-b075-bbe01348cefd0.MirrorCS");var subQ1=sQuery(id+"F1.wireOp",EDGE,"11422904-8dbc-437f-b2cb-607545d81d6e.0");var subQ2=makeQuery(id+"F1.imprint","INTERSECT",VERTEX,{"derivedFrom":[subQ1,subQ0]});Q100=makeQuery(id+"F1.imprint","IMPRINT",FACE,{"disambiguationData":[TD([[makeQuery(id+"F1.imprint","IMPRINT",EDGE,{"disambiguationData":[TD([[subQ2,-1.0]])],"derivedFrom":subQ1}),1.0]])]});}
            var Q101;
            {var subQ4=sQuery(id+"F0.wireOp",EDGE,"E26");Q101=makeQuery(id+"F0.imprint","IMPRINT",FACE,{"disambiguationData":[TD([[makeQuery(id+"F0.imprint","IMPRINT",EDGE,{"derivedFrom":subQ4}),1.0]])]});}
            extrude(context, id + "F2", {"entities" : qUnion([Q0, Q1, Q2, Q3, Q4, Q5, Q6, Q7, Q8, Q9, Q10, Q11, Q12, Q13, Q14, Q15, Q16, Q17, Q18, Q19, Q20, Q21, Q22, Q23, Q24, Q25, Q26, Q27, Q28, Q29, Q30, Q31, Q32, Q33, Q34, Q35, Q36, Q37, Q38, Q39, Q40, Q41, Q42, Q43, Q44, Q45, Q46, Q47, Q48, Q49, Q50, Q51, Q52, Q53, Q54, Q55, Q56, Q57, Q58, Q59, Q60, Q61, Q62, Q63, Q64, Q65, Q66, Q67, Q68, Q69, Q70, Q71, Q72, Q73, Q74, Q75, Q76, Q77, Q78, Q79, Q80, Q81, Q82, Q83, Q84, Q85, Q86, Q87, Q88, Q89, Q90, Q91, Q92, Q93, Q94, Q95, Q96, Q97, Q98, Q99, Q100, Q101]), "depth" : 0.2 * mm});
        }
    });
